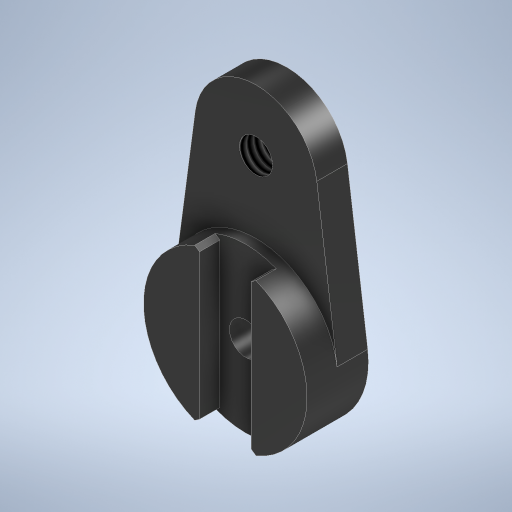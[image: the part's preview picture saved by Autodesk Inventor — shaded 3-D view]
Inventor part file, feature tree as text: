
AUTODESK INVENTOR PART (.ipt)
format: ipt  version: 2024.2 (Build 282272000, 272)  size: 290,816 bytes
history: native  units: mm
features: extrude x3, sketch x1, hole x1, chamfer x1
ambient origin geometry x8: Origin, YZ Plane, XZ Plane, XY Plane, X Axis, Y Axis, Z Axis, Center Point
bodies: Solid1 (feature_tree)
feature tree (6):
  sketch  "Sketch1"  dims[d0=16.0mm d1=15.0mm d2=12.0mm d3=5.0mm d4=0.025mm d5=6.0mm d6=0.0mm d7=2.0mm d8=0.0mm d9=3.0mm d10=0.0mm d11=3.2mm d12=6.0mm d13=4.0mm d14=2.0mm d15=90.0deg d16=8.0mm d17=20.594885mm d18=3.242mm d19=8.0mm d20=4.0mm d21=2.0mm d22=90.0deg d23=8.0mm d24=20.594885mm d25=0.5mm d26=2.0mm d27=45.0deg d28=20.0mm d30=90.0deg]
  extrude  "Extrusion1"  Depth=15.0mm
  extrude  "Extrusion2"  Depth=2.0mm
  extrude  "Extrusion3"  Depth=2.0mm
  hole  "Phi3.2"  [1 undecoded]
  chamfer  "C0.5"  Distance=6.0mm
note: 1 required parameter value undecoded (feature->parameter linkage not recoverable at this tier; creation-order binding heuristic only, values carry confidence <= 0.55)
